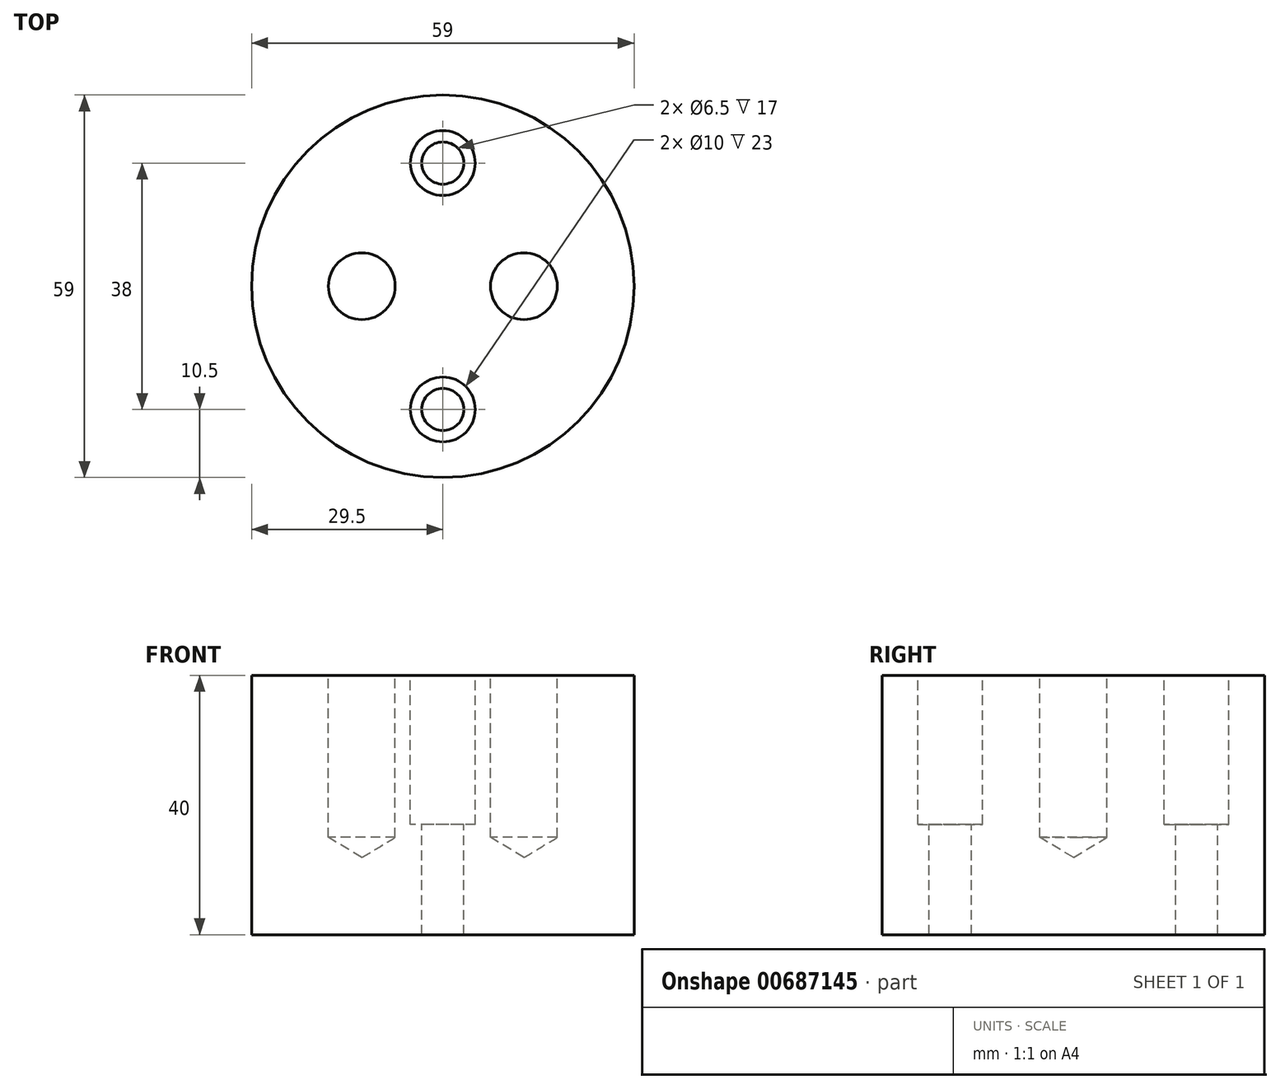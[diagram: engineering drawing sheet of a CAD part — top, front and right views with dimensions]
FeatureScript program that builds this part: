
annotation { "Feature Type Name" : "Feature", "Feature Type Description" : "" }
export const myFeature = defineFeature(function(context is Context, id is Id, definition is map)
    precondition{}
    {
        {
            var Q0;
            Q0=qCreatedBy(makeId("Top.planeOp"),FACE);
            var sketch = newSketch(context, id + "F0", { "sketchPlane" : qUnion([Q0])});
            skCircle(sketch, "E0", {"center": v(0, 0) * mm, "radius": 29.5 * mm});
            skSolve(sketch);
        }
        {
            var Q0;
            Q0 = qSketchRegion(id + "F0", true);
            extrude(context, id + "F1", {"entities" : qUnion([Q0]), "depth" : 40 * mm, "offsetDistance" : 25 * mm});
        }
        {
            var Q0;
            Q0=makeQuery(id+"F1.opExtrude","CAP_FACE",FACE,{"disambiguationData":[OSD([sQuery(id+"F0.wireOp",EDGE,"E0"),sQuery(id+"F0.wireOp",EDGE,"Ul7NDqZO-m4rh-qcKf-VXfJ-OEDmdI6x9r66"),sQuery(id+"F0.wireOp",EDGE,"WJgXlw0m-8zfw-uin1-PerT-Y9pHDMGgwseE")])],"isStart":false});
            var sketch = newSketch(context, id + "F2", { "sketchPlane" : qUnion([Q0])});
            skPoint(sketch, "E1", {"position": v(-12.5, 0) * mm});
            skPoint(sketch, "E2", {"position": v(12.5, 0) * mm});
            skSolve(sketch);
        }
        {
            var Q0;
            Q0=sQuery(id+"F2.wireOp",VERTEX,"E1");
            var Q1;
            Q1=sQuery(id+"F2.wireOp",VERTEX,"E2");
            var Q2;
            Q2=makeQuery(id+"F1.opExtrude","SWEPT_BODY",BODY,{"disambiguationData":[OSD([sQuery(id+"F0.wireOp",EDGE,"E0"),sQuery(id+"F0.wireOp",EDGE,"Ul7NDqZO-m4rh-qcKf-VXfJ-OEDmdI6x9r66"),sQuery(id+"F0.wireOp",EDGE,"WJgXlw0m-8zfw-uin1-PerT-Y9pHDMGgwseE")])]});
            hole(context, id + "F3", {"style" : HoleStyle.SIMPLE, "endStyle" : HoleEndStyle.BLIND, "standardTappedOrClearance" : lookupTablePath({ "standard" : "ISO", "engagement" : "75%", "pitch" : "1.75 mm", "size" : "M12", "type" : "Tapped" }), "standardBlindInLast" : lookupTablePath({ "standard" : "ISO", "engagement" : "75%", "pitch" : "1.75 mm", "size" : "M12", "type" : "Tapped" }), "holeDiameter" : 10.3 * mm, "majorDiameter" : 12 * mm, "showTappedDepth" : true, "holeDepth" : 25 * mm, "isTappedThrough" : true, "tappedDepth" : 19.75 * mm, "tapClearance" : 3, "startFromSketch" : true, "locations" : qUnion([Q0, Q1]), "scope" : qUnion([Q2])});
        }
        {
            var Q0;
            Q0=makeQuery(id+"F1.opExtrude","CAP_FACE",FACE,{"disambiguationData":[OSD([sQuery(id+"F0.wireOp",EDGE,"E0")])],"isStart":false});
            var sketch = newSketch(context, id + "F4", { "sketchPlane" : qUnion([Q0])});
            skPoint(sketch, "E3", {"position": v(0, 19) * mm});
            skPoint(sketch, "E4", {"position": v(0, -19) * mm});
            skSolve(sketch);
        }
        {
            var Q0;
            Q0=sQuery(id+"F4.wireOp",VERTEX,"E3");
            var Q1;
            Q1=sQuery(id+"F4.wireOp",VERTEX,"E4");
            var Q2;
            Q2=makeQuery(id+"F1.opExtrude","SWEPT_BODY",BODY,{"disambiguationData":[OSD([sQuery(id+"F0.wireOp",EDGE,"E0")])]});
            hole(context, id + "F5", {"style" : HoleStyle.C_BORE, "endStyle" : HoleEndStyle.THROUGH, "holeDiameter" : 6.5 * mm, "cBoreDiameter" : 10 * mm, "cBoreDepth" : 23 * mm, "majorDiameter" : 12 * mm, "isTappedThrough" : true, "tappedDepth" : 19.75 * mm, "tapClearance" : 3, "startFromSketch" : true, "locations" : qUnion([Q0, Q1]), "scope" : qUnion([Q2])});
        }
    });
